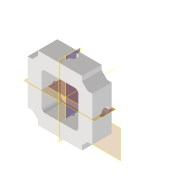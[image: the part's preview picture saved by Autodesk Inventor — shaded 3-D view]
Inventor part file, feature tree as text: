
AUTODESK INVENTOR PART (.ipt)
format: ipt  version: 2022 (Build 260153000, 153)  size: 224,768 bytes
history: native  units: mm
features: plane x7, extrude x3, sketch x3, other x3, projected_geometry x2, hole x1, pattern_circular x1, reference x1
ambient origin geometry x8: Origin, YZ Plane, XZ Plane, XY Plane, X Axis, Y Axis, Z Axis, Center Point
bodies: Solid1 (feature_tree)
feature tree (21):
  plane  "Work Plane5"
  extrude  "Extrusion1"  Depth=15.0mm
  extrude  "IM_offset"  Depth=53.8mm
  extrude  "Extrusion23"  Depth=4.0mm
  sketch  "Sketch30"  dims[d21=45.0mm d22=45.0mm d30=20.0mm d31=20.0mm d32=2.8mm d33=2.8mm d34=2.8mm d35=3.0mm d36=0.1mm d37=0.1mm d38=0.1mm d39=0.1mm d40=0.2mm d41=10.0mm d42=0.0mm d172=10.0mm d173=0.0mm d176=0.2mm d177=2.8mm d178=6.0mm d179=6.0mm d180=4.0mm d181=90.0deg d182=8.0mm d183=20.594885mm d184=40.0mm d185=360.0deg]
  plane  "Arbeitsebene7"
  plane  "Arbeitsebene8"
  plane  "Arbeitsebene9"
  plane  "Arbeitsebene10"
  hole  "Bohrung2"  [1 undecoded]
  other  "Arbeitsachse1"
  pattern_circular  "Runde Anordnung2"  Count=2  [1 undecoded]
  plane  "Arbeitsebene11"
  plane  "Arbeitsebene12"
  sketch  "Sketch1"  dims[d10=15.0mm d11=0.0mm d18=53.8mm]
  sketch  "Skizze4"  dims[d19=45.0deg d20=53.8mm]
  projected_geometry  "Projizierte Kontur1"
  reference  "Referenz29"
  projected_geometry  "Projizierte Kontur18"
  other  "Assembly_Cube_Z_Focus_MGN_NEMA_belt_v3.iam"
  other  "00_NEMA11:1"
note: 2 required parameter values undecoded (feature->parameter linkage not recoverable at this tier; creation-order binding heuristic only, values carry confidence <= 0.55)
